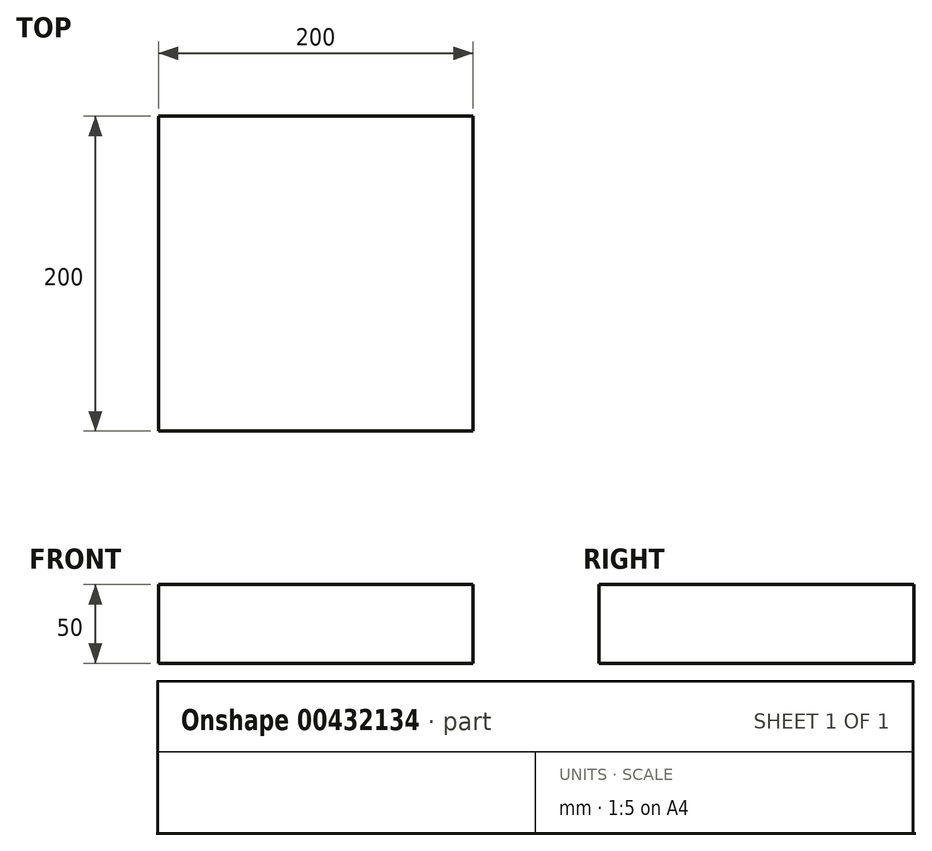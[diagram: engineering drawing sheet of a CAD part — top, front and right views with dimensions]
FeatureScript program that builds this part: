
annotation { "Feature Type Name" : "Feature", "Feature Type Description" : "" }
export const myFeature = defineFeature(function(context is Context, id is Id, definition is map)
    precondition{}
    {
        {
            var Q0;
            Q0=qCreatedBy(makeId("Top.planeOp"),FACE);
            var sketch = newSketch(context, id + "F0", { "sketchPlane" : qUnion([Q0])});
            skLineSegment(sketch, "E0.bottom", {"start": v(-83.23, 127.08) * mm, "end": v(116.77, 127.08) * mm});
            skLineSegment(sketch, "E0.top", {"start": v(-83.23, -72.92) * mm, "end": v(116.77, -72.92) * mm});
            skLineSegment(sketch, "E0.left", {"start": v(-83.23, 127.08) * mm, "end": v(-83.23, -72.92) * mm});
            skLineSegment(sketch, "E0.right", {"start": v(116.77, 127.08) * mm, "end": v(116.77, -72.92) * mm});
            skSolve(sketch);
        }
        {
            var Q0;
            Q0=makeQuery(id+"F0.imprint","IMPRINT",FACE,{"disambiguationData":[TD([[makeQuery(id+"F0.imprint","IMPRINT",EDGE,{"derivedFrom":sQuery(id+"F0.wireOp",EDGE,"E0.bottom")}),-1.0]])]});
            extrude(context, id + "F1", {"entities" : qUnion([Q0]), "depth" : 50 * mm});
        }
    });
